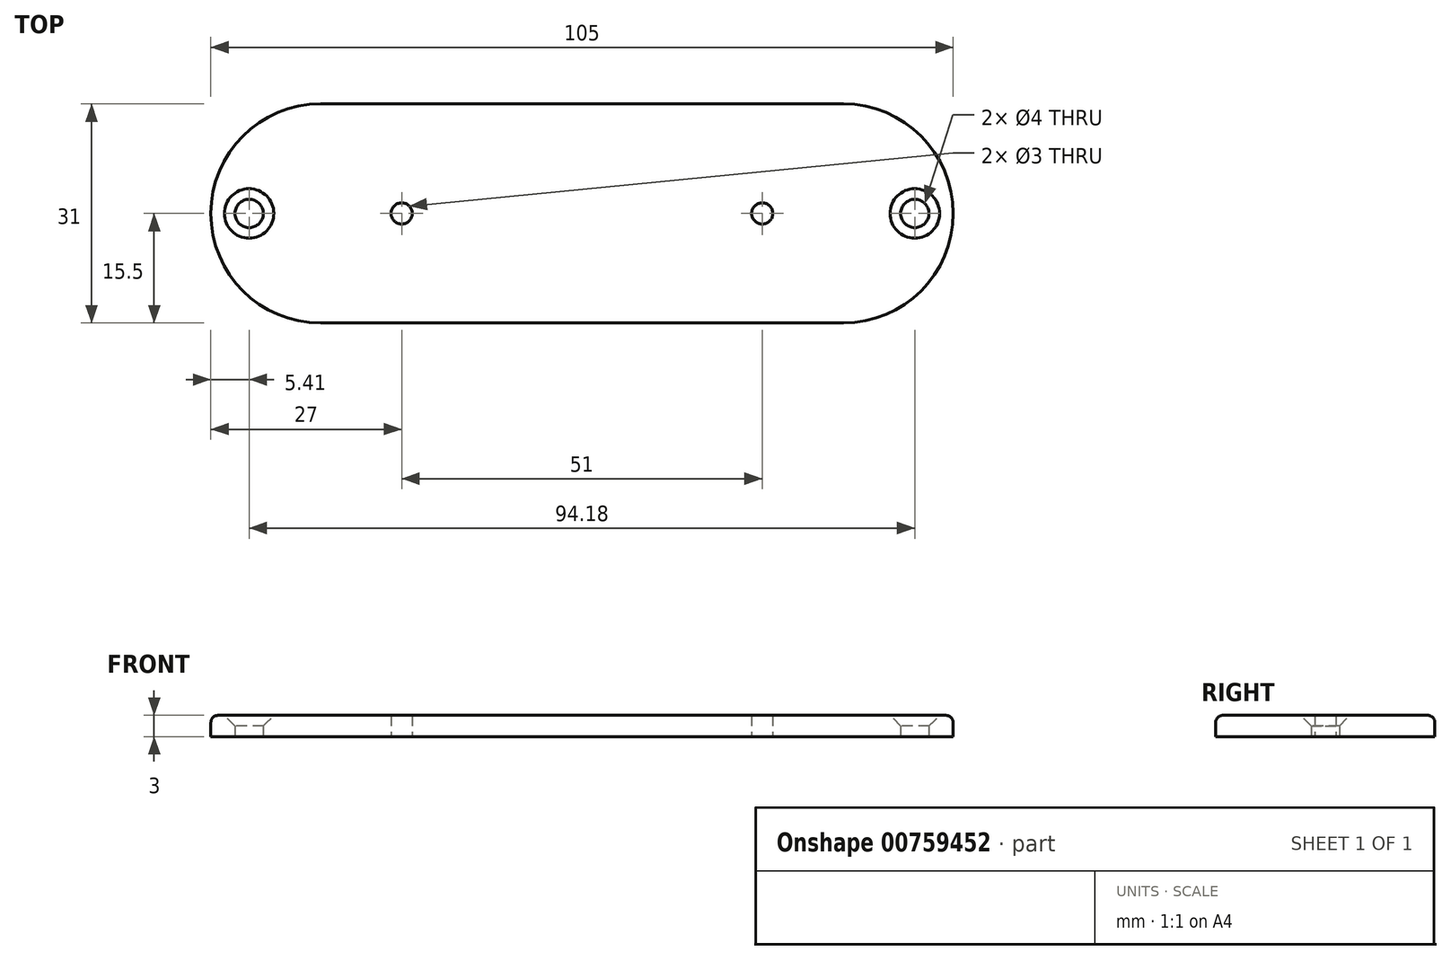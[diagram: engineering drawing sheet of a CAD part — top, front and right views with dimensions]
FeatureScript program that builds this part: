
annotation { "Feature Type Name" : "Feature", "Feature Type Description" : "" }
export const myFeature = defineFeature(function(context is Context, id is Id, definition is map)
    precondition{}
    {
        {
            var Q0;
            Q0=qCreatedBy(makeId("Top.planeOp"),FACE);
            var sketch = newSketch(context, id + "F0", { "sketchPlane" : qUnion([Q0])});
            skLineSegment(sketch, "E0.bottom", {"start": v(37, 15.5) * mm, "end": v(-37, 15.5) * mm});
            skLineSegment(sketch, "E0.top", {"start": v(37, -15.5) * mm, "end": v(-37, -15.5) * mm});
            skPoint(sketch, "E0.middle", {"position": v(0, 0) * mm});
            skArc(sketch, "E1", {"start": v(-37, -15.5) * mm, "mid": v(-52.5, 0) * mm, "end": v(-37, 15.5) * mm});
            skArc(sketch, "E2.MirrorCS", {"start": v(37, -15.5) * mm, "mid": v(52.5, 0) * mm, "end": v(37, 15.5) * mm});
            skCircle(sketch, "E3", {"center": v(-47.1, 0) * mm, "radius": 2 * mm});
            skCircle(sketch, "E4", {"center": v(-25.5, 0) * mm, "radius": 1.5 * mm});
            skCircle(sketch, "E5.MirrorC", {"center": v(25.5, 0) * mm, "radius": 1.5 * mm});
            skCircle(sketch, "E6.MirrorC", {"center": v(47.1, 0) * mm, "radius": 2 * mm});
            skSolve(sketch);
        }
        {
            var Q0;
            Q0=makeQuery(id+"F0.imprint","IMPRINT",FACE,{"disambiguationData":[TD([[makeQuery(id+"F0.imprint","IMPRINT",EDGE,{"derivedFrom":sQuery(id+"F0.wireOp",EDGE,"E0.bottom")}),1.0]])]});
            extrude(context, id + "F1", {"entities" : qUnion([Q0]), "depth" : 3 * mm, "offsetDistance" : 25 * mm});
        }
        {
            var Q0;
            Q0=makeQuery(id+"F1.opExtrude","CAP_EDGE",EDGE,{"disambiguationData":[OSD([sQuery(id+"F0.wireOp",EDGE,"E2.MirrorCS")])],"isStart":false});
            fillet(context, id + "F2", {"entities" : qUnion([Q0]), "radius" : 1 * mm, "tangentPropagation" : true, "allowEdgeOverflow" : false});
        }
        {
            var Q0;
            Q0=makeQuery(id+"F1.opExtrude","CAP_EDGE",EDGE,{"disambiguationData":[OSD([sQuery(id+"F0.wireOp",EDGE,"E6.MirrorC")])],"isStart":false});
            var Q1;
            Q1=makeQuery(id+"F1.opExtrude","CAP_EDGE",EDGE,{"disambiguationData":[OSD([sQuery(id+"F0.wireOp",EDGE,"E3")])],"isStart":false});
            chamfer(context, id + "F3", {"entities" : qUnion([Q0, Q1]), "width" : 1.5 * mm, "tangentPropagation" : true});
        }
    });
